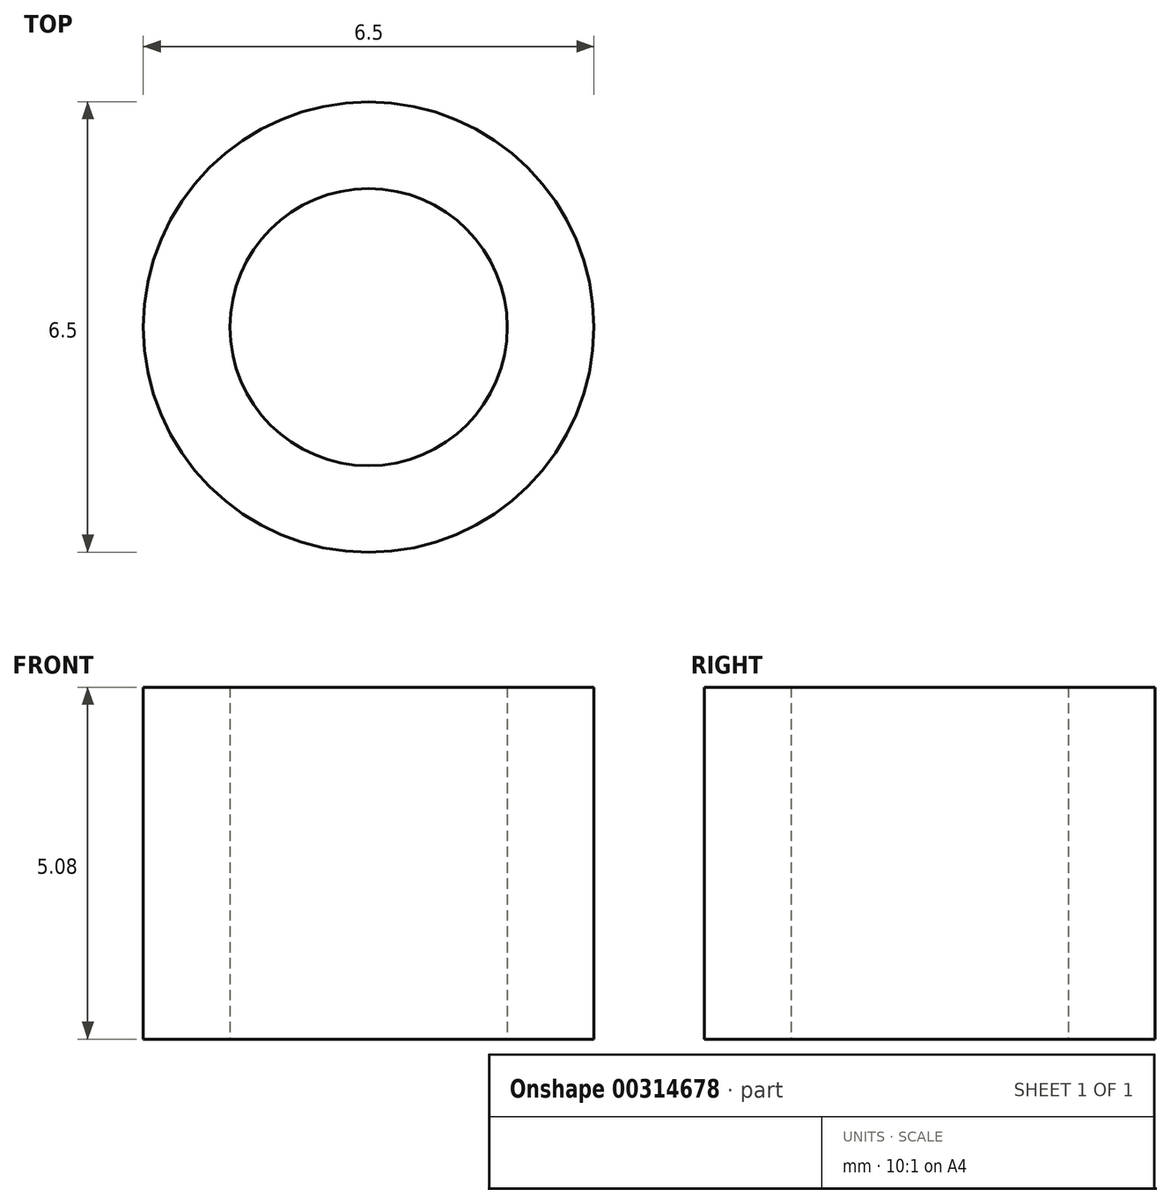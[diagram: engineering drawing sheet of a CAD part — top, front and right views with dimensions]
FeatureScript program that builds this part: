
annotation { "Feature Type Name" : "Feature", "Feature Type Description" : "" }
export const myFeature = defineFeature(function(context is Context, id is Id, definition is map)
    precondition{}
    {
        {
            var Q0;
            Q0=qCreatedBy(makeId("Top.planeOp"),FACE);
            var sketch = newSketch(context, id + "F0", { "sketchPlane" : qUnion([Q0])});
            skCircle(sketch, "E0", {"center": v(-56.18, 34.75) * mm, "radius": 3.25 * mm});
            skCircle(sketch, "E1", {"center": v(-56.18, 34.75) * mm, "radius": 2 * mm});
            skSolve(sketch);
        }
        {
            var Q0;
            Q0 = qSketchRegion(id + "F0", true);
            extrude(context, id + "F1", {"entities" : qUnion([Q0]), "depth" : 5.08 * mm});
        }
    });
